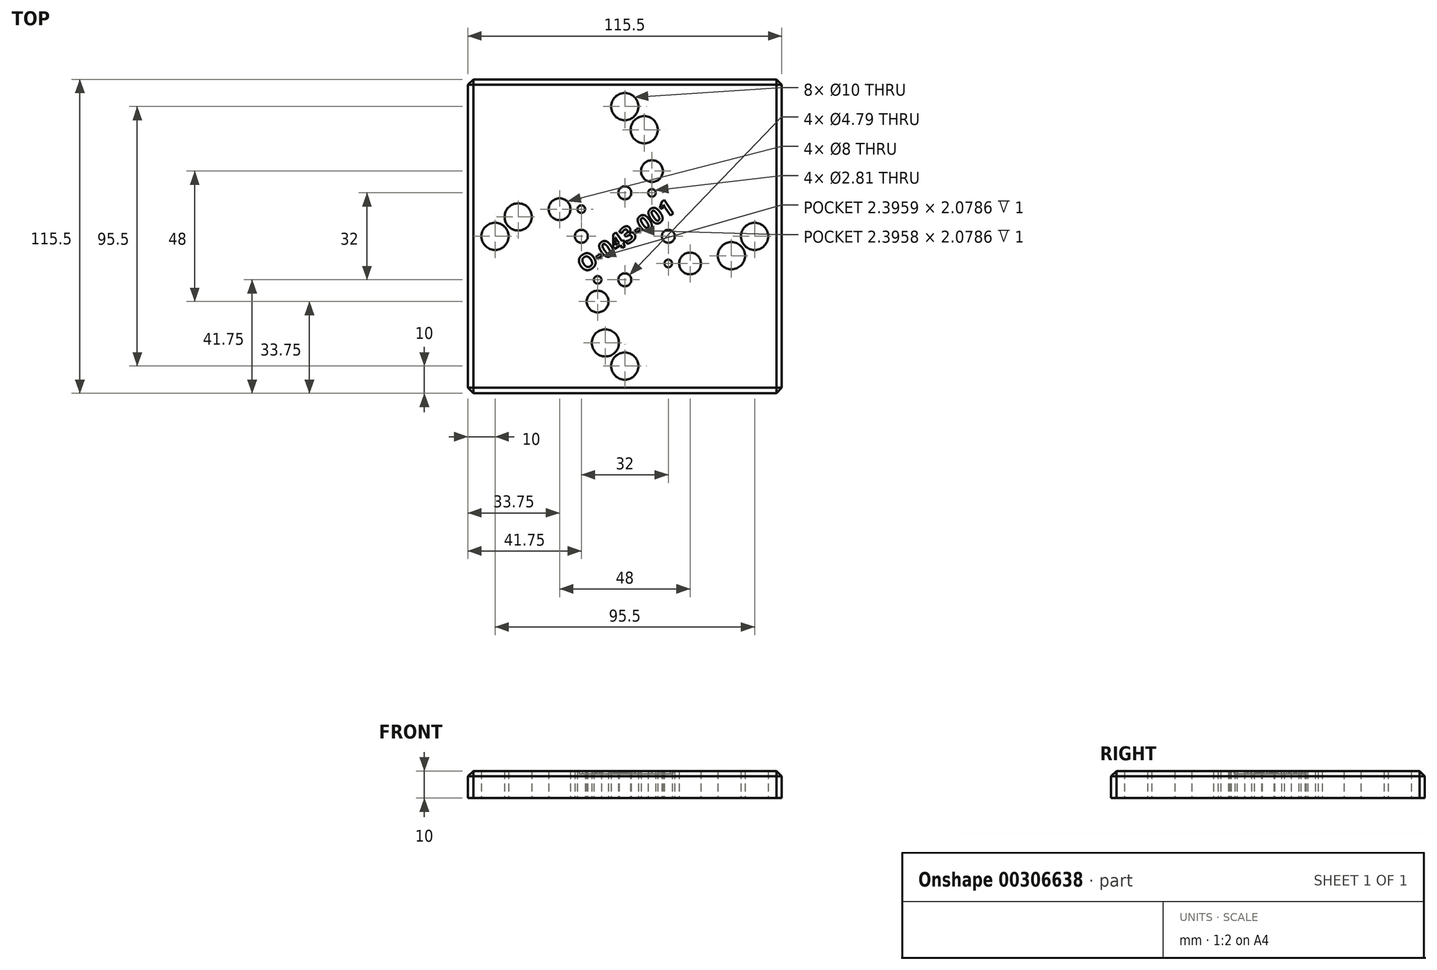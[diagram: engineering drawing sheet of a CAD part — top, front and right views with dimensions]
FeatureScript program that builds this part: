
annotation { "Feature Type Name" : "Feature", "Feature Type Description" : "" }
export const myFeature = defineFeature(function(context is Context, id is Id, definition is map)
    precondition{}
    {
        {
            var Q0;
            Q0=qCreatedBy(makeId("Top.planeOp"),FACE);
            var sketch = newSketch(context, id + "F0", { "sketchPlane" : qUnion([Q0])});
            skCircle(sketch, "E0", {"center": v(-16, 0) * mm, "radius": 2.4 * mm});
            skPoint(sketch, "E1", {"position": v(-16, 10) * mm});
            skCircle(sketch, "E2", {"center": v(-24, 10) * mm, "radius": 4 * mm});
            skCircle(sketch, "E3", {"center": v(-47.75, 0) * mm, "radius": 5 * mm});
            skCircle(sketch, "E4", {"center": v(-70.98, -2.85) * mm, "radius": 1.4 * mm, "construction": true});
            skLineSegment(sketch, "E5", {"start": v(-70.98, -2.85) * mm, "end": v(-24.45, 2.86) * mm, "construction": true});
            skArc(sketch, "E6", {"start": v(-16, -6) * mm, "mid": v(-11.76, -4.24) * mm, "end": v(-10, 0) * mm, "construction": true});
            skLineSegment(sketch, "E7", {"start": v(-10, 0) * mm, "end": v(-10, 10) * mm, "construction": true});
            skArc(sketch, "E8", {"start": v(-10, 10) * mm, "mid": v(-11.76, 14.24) * mm, "end": v(-16, 16) * mm, "construction": true});
            skLineSegment(sketch, "E9", {"start": v(-16, 16) * mm, "end": v(-24, 16) * mm, "construction": true});
            skLineSegment(sketch, "E10.1.0", {"start": v(0, -10) * mm, "end": v(-10, -10) * mm, "construction": true});
            skArc(sketch, "E10.1.1", {"start": v(6, -16) * mm, "mid": v(4.24, -11.76) * mm, "end": v(0, -10) * mm, "construction": true});
            skCircle(sketch, "E10.1.2", {"center": v(0, -16) * mm, "radius": 2.4 * mm});
            skArc(sketch, "E10.1.3", {"start": v(-10, -10) * mm, "mid": v(-14.24, -11.76) * mm, "end": v(-16, -16) * mm, "construction": true});
            skLineSegment(sketch, "E10.1.4", {"start": v(-16, -16) * mm, "end": v(-16, -24) * mm, "construction": true});
            skPoint(sketch, "E10.1.5", {"position": v(-10, -16) * mm});
            skCircle(sketch, "E10.1.6", {"center": v(-10, -24) * mm, "radius": 4 * mm});
            skCircle(sketch, "E10.1.7", {"center": v(0, -47.75) * mm, "radius": 5 * mm});
            skLineSegment(sketch, "E10.1.8", {"start": v(2.85, -70.98) * mm, "end": v(-2.86, -24.45) * mm, "construction": true});
            skCircle(sketch, "E10.1.9", {"center": v(2.85, -70.98) * mm, "radius": 1.4 * mm, "construction": true});
            skLineSegment(sketch, "E10.2.0", {"start": v(10, 0) * mm, "end": v(10, -10) * mm, "construction": true});
            skArc(sketch, "E10.2.1", {"start": v(16, 6) * mm, "mid": v(11.76, 4.24) * mm, "end": v(10, 0) * mm, "construction": true});
            skCircle(sketch, "E10.2.2", {"center": v(16, 0) * mm, "radius": 2.4 * mm});
            skArc(sketch, "E10.2.3", {"start": v(10, -10) * mm, "mid": v(11.76, -14.24) * mm, "end": v(16, -16) * mm, "construction": true});
            skLineSegment(sketch, "E10.2.4", {"start": v(16, -16) * mm, "end": v(24, -16) * mm, "construction": true});
            skPoint(sketch, "E10.2.5", {"position": v(16, -10) * mm});
            skCircle(sketch, "E10.2.6", {"center": v(24, -10) * mm, "radius": 4 * mm});
            skCircle(sketch, "E10.2.7", {"center": v(47.75, 0) * mm, "radius": 5 * mm});
            skLineSegment(sketch, "E10.2.8", {"start": v(70.98, 2.85) * mm, "end": v(24.45, -2.86) * mm, "construction": true});
            skCircle(sketch, "E10.2.9", {"center": v(70.98, 2.85) * mm, "radius": 1.4 * mm, "construction": true});
            skLineSegment(sketch, "E10.3.0", {"start": v(0, 10) * mm, "end": v(10, 10) * mm});
            skArc(sketch, "E10.3.1", {"start": v(-6, 16) * mm, "mid": v(-4.24, 11.76) * mm, "end": v(0, 10) * mm});
            skCircle(sketch, "E10.3.2", {"center": v(0, 16) * mm, "radius": 2.4 * mm});
            skArc(sketch, "E10.3.3", {"start": v(10, 10) * mm, "mid": v(14.24, 11.76) * mm, "end": v(16, 16) * mm});
            skLineSegment(sketch, "E10.3.4", {"start": v(16, 16) * mm, "end": v(16, 24) * mm});
            skPoint(sketch, "E10.3.5", {"position": v(10, 16) * mm});
            skCircle(sketch, "E10.3.6", {"center": v(10, 24) * mm, "radius": 4 * mm});
            skCircle(sketch, "E10.3.7", {"center": v(0, 47.75) * mm, "radius": 5 * mm});
            skLineSegment(sketch, "E10.3.8", {"start": v(-2.85, 70.98) * mm, "end": v(2.86, 24.45) * mm, "construction": true});
            skCircle(sketch, "E10.3.9", {"center": v(-2.85, 70.98) * mm, "radius": 1.4 * mm, "construction": true});
            skPoint(sketch, "E10.center", {"position": v(0, 0) * mm});
            skCircle(sketch, "E11", {"center": v(16, -10) * mm, "radius": 1.4 * mm});
            skCircle(sketch, "E12", {"center": v(39.23, -7.15) * mm, "radius": 5 * mm});
            skCircle(sketch, "E13", {"center": v(70.98, -7.15) * mm, "radius": 2.4 * mm, "construction": true});
            skLineSegment(sketch, "E14", {"start": v(16, -10) * mm, "end": v(44.43, -6.5) * mm, "construction": true});
            skLineSegment(sketch, "E15", {"start": v(39.23, -7.15) * mm, "end": v(70.98, -7.15) * mm, "construction": true});
            skArc(sketch, "E16", {"start": v(16, -6.3) * mm, "mid": v(13.38, -7.38) * mm, "end": v(12.3, -10) * mm, "construction": true});
            skCircle(sketch, "E17", {"center": v(62.98, 2.85) * mm, "radius": 4 * mm, "construction": true});
            skCircle(sketch, "E18.1.0", {"center": v(10, 16) * mm, "radius": 1.4 * mm});
            skCircle(sketch, "E18.1.1", {"center": v(7.15, 39.23) * mm, "radius": 5 * mm});
            skCircle(sketch, "E18.1.2", {"center": v(7.15, 70.98) * mm, "radius": 2.4 * mm, "construction": true});
            skCircle(sketch, "E18.1.3", {"center": v(-2.85, 62.98) * mm, "radius": 4 * mm, "construction": true});
            skCircle(sketch, "E18.2.0", {"center": v(-16, 10) * mm, "radius": 1.4 * mm});
            skCircle(sketch, "E18.2.1", {"center": v(-39.23, 7.15) * mm, "radius": 5 * mm});
            skCircle(sketch, "E18.2.2", {"center": v(-70.98, 7.15) * mm, "radius": 2.4 * mm, "construction": true});
            skCircle(sketch, "E18.2.3", {"center": v(-62.98, -2.85) * mm, "radius": 4 * mm, "construction": true});
            skCircle(sketch, "E18.3.0", {"center": v(-10, -16) * mm, "radius": 1.4 * mm});
            skCircle(sketch, "E18.3.1", {"center": v(-7.15, -39.23) * mm, "radius": 5 * mm});
            skCircle(sketch, "E18.3.2", {"center": v(-7.15, -70.98) * mm, "radius": 2.4 * mm, "construction": true});
            skCircle(sketch, "E18.3.3", {"center": v(2.85, -62.98) * mm, "radius": 4 * mm, "construction": true});
            skLineSegment(sketch, "E19", {"start": v(-21, -57.75) * mm, "end": v(10, -57.75) * mm});
            skLineSegment(sketch, "E20", {"start": v(57.75, -21) * mm, "end": v(57.75, 10) * mm});
            skLineSegment(sketch, "E21", {"start": v(21, 57.75) * mm, "end": v(-10, 57.75) * mm});
            skCircle(sketch, "E22", {"center": v(0, 0) * mm, "radius": 25 * mm, "construction": true});
            skLineSegment(sketch, "E23.bottom", {"start": v(-57.75, 57.75) * mm, "end": v(57.75, 57.75) * mm});
            skLineSegment(sketch, "E23.top", {"start": v(-57.75, -57.75) * mm, "end": v(57.75, -57.75) * mm});
            skLineSegment(sketch, "E23.left", {"start": v(-57.75, 57.75) * mm, "end": v(-57.75, -57.75) * mm});
            skLineSegment(sketch, "E23.right", {"start": v(57.75, 57.75) * mm, "end": v(57.75, -57.75) * mm});
            skLineSegment(sketch, "E24.trimOffspring", {"start": v(-57.75, -57.75) * mm, "end": v(-57.75, -57.75) * mm});
            skLineSegment(sketch, "E25", {"start": v(16, -10) * mm, "end": v(0, 0) * mm, "construction": true});
            skLineSegment(sketch, "E26", {"start": v(24, -10) * mm, "end": v(0, 0) * mm, "construction": true});
            skLineSegment(sketch, "E27", {"start": v(0, 0) * mm, "end": v(39.23, -7.15) * mm, "construction": true});
            skSolve(sketch);
        }
        {
            var Q0;
            Q0=makeQuery(id+"F0.imprint","IMPRINT",FACE,{"disambiguationData":[TD([[makeQuery(id+"F0.imprint","IMPRINT",EDGE,{"derivedFrom":sQuery(id+"F0.wireOp",EDGE,"E0")}),-1.0]])]});
            extrude(context, id + "F1", {"entities" : qUnion([Q0]), "depth" : 10 * mm});
        }
        {
            var Q0;
            Q0=makeQuery(id+"F1.opExtrude","CAP_FACE",FACE,{"disambiguationData":[OSD([sQuery(id+"F0.wireOp",EDGE,"E0"),sQuery(id+"F0.wireOp",EDGE,"E2"),sQuery(id+"F0.wireOp",EDGE,"E3"),sQuery(id+"F0.wireOp",EDGE,"E10.1.2"),sQuery(id+"F0.wireOp",EDGE,"E10.1.6"),sQuery(id+"F0.wireOp",EDGE,"E10.1.7"),sQuery(id+"F0.wireOp",EDGE,"E10.2.2"),sQuery(id+"F0.wireOp",EDGE,"E10.2.6"),sQuery(id+"F0.wireOp",EDGE,"E10.2.7"),sQuery(id+"F0.wireOp",EDGE,"E10.3.2"),sQuery(id+"F0.wireOp",EDGE,"E10.3.6"),sQuery(id+"F0.wireOp",EDGE,"E10.3.7"),sQuery(id+"F0.wireOp",EDGE,"E11"),sQuery(id+"F0.wireOp",EDGE,"E12"),sQuery(id+"F0.wireOp",EDGE,"E18.1.0"),sQuery(id+"F0.wireOp",EDGE,"E18.1.1"),sQuery(id+"F0.wireOp",EDGE,"E18.2.0"),sQuery(id+"F0.wireOp",EDGE,"E18.2.1"),sQuery(id+"F0.wireOp",EDGE,"E18.3.0"),sQuery(id+"F0.wireOp",EDGE,"E18.3.1"),sQuery(id+"F0.wireOp",EDGE,"MyoJIBSz-K6gS-HFCk-aKoN-saKFs5IhSE7Z"),sQuery(id+"F0.wireOp",EDGE,"1NPSEbLD-hnYt-Wvdz-GnfD-U5UPild5qYg3"),sQuery(id+"F0.wireOp",EDGE,"pjWNRYpZ-PtQu-NHhX-2XcQ-7lOy1gO7q9jb"),sQuery(id+"F0.wireOp",EDGE,"E19"),sQuery(id+"F0.wireOp",EDGE,"Gumg3WsQ-Ub7a-efM0-DFZZ-8XctyF9TNLiq"),sQuery(id+"F0.wireOp",EDGE,"s1G268Qx-9Fw0-vXF1-vVHZ-y5ZcVpehrivC"),sQuery(id+"F0.wireOp",EDGE,"E20"),sQuery(id+"F0.wireOp",EDGE,"Q10wiKAX-9aoS-ymFz-mVGt-GhKXSLZOkAHw"),sQuery(id+"F0.wireOp",EDGE,"l82vxAns-bnEz-TrX4-Njma-a1FynIs3hUHN"),sQuery(id+"F0.wireOp",EDGE,"E21"),sQuery(id+"F0.wireOp",EDGE,"H0JYGMW6-TGJH-diSg-jyGy-scULVfW25UrG"),sQuery(id+"F0.wireOp",EDGE,"yQtjxce7-IDGc-WV1h-hYuQ-jwLA51wQaN9m")])],"isStart":false});
            var sketch = newSketch(context, id + "F2", { "sketchPlane" : qUnion([Q0])});
            skText(sketch, "E28", { "text": "O-043-001", "fontName": "OpenSans-Bold.ttf"});
            skPoint(sketch, "E29", {"position": v(0, 0) * mm});
            const initialGuessF2  = {"E28": [-0.0149, -0.01369, 0.82904, 0.5592, 0.00604]};
            skSetInitialGuess(sketch, initialGuessF2);
            skSolve(sketch);
        }
        {
            var Q0;
            Q0 = qSketchRegion(id + "F2", true);
            extrude(context, id + "F3", {"entities" : qUnion([Q0]), "operationType" : NewBodyOperationType.REMOVE, "oppositeDirection" : true, "depth" : 1 * mm});
        }
        {
            var Q0;
            Q0=makeQuery(id+"F1.opExtrude","SWEPT_EDGE",EDGE,{"disambiguationData":[OSD([sQuery(id+"F0.wireOp",EDGE,"E23.top"),sQuery(id+"F0.wireOp",EDGE,"E23.left")])]});
            var Q1;
            Q1=makeQuery(id+"F1.opExtrude","SWEPT_EDGE",EDGE,{"disambiguationData":[OSD([sQuery(id+"F0.wireOp",EDGE,"E23.top"),sQuery(id+"F0.wireOp",EDGE,"E23.right")])]});
            var Q2;
            Q2=makeQuery(id+"F1.opExtrude","SWEPT_EDGE",EDGE,{"disambiguationData":[OSD([sQuery(id+"F0.wireOp",EDGE,"E23.bottom"),sQuery(id+"F0.wireOp",EDGE,"E23.right")])]});
            var Q3;
            Q3=makeQuery(id+"F1.opExtrude","SWEPT_EDGE",EDGE,{"disambiguationData":[OSD([sQuery(id+"F0.wireOp",EDGE,"E23.bottom"),sQuery(id+"F0.wireOp",EDGE,"E23.left")])]});
            var Q4;
            Q4=makeQuery(id+"F1.opExtrude","CAP_EDGE",EDGE,{"disambiguationData":[OSD([sQuery(id+"F0.wireOp",EDGE,"E23.bottom")])],"isStart":false});
            var Q5;
            Q5=makeQuery(id+"F1.opExtrude","CAP_EDGE",EDGE,{"disambiguationData":[OSD([sQuery(id+"F0.wireOp",EDGE,"E23.right")])],"isStart":false});
            var Q6;
            Q6=makeQuery(id+"F1.opExtrude","CAP_EDGE",EDGE,{"disambiguationData":[OSD([sQuery(id+"F0.wireOp",EDGE,"E23.top")])],"isStart":false});
            var Q7;
            Q7=makeQuery(id+"F1.opExtrude","CAP_EDGE",EDGE,{"disambiguationData":[OSD([sQuery(id+"F0.wireOp",EDGE,"E23.left")])],"isStart":false});
            chamfer(context, id + "F4", {"entities" : qUnion([Q0, Q1, Q2, Q3, Q4, Q5, Q6, Q7]), "width" : 2 * mm, "tangentPropagation" : true});
        }
    });
